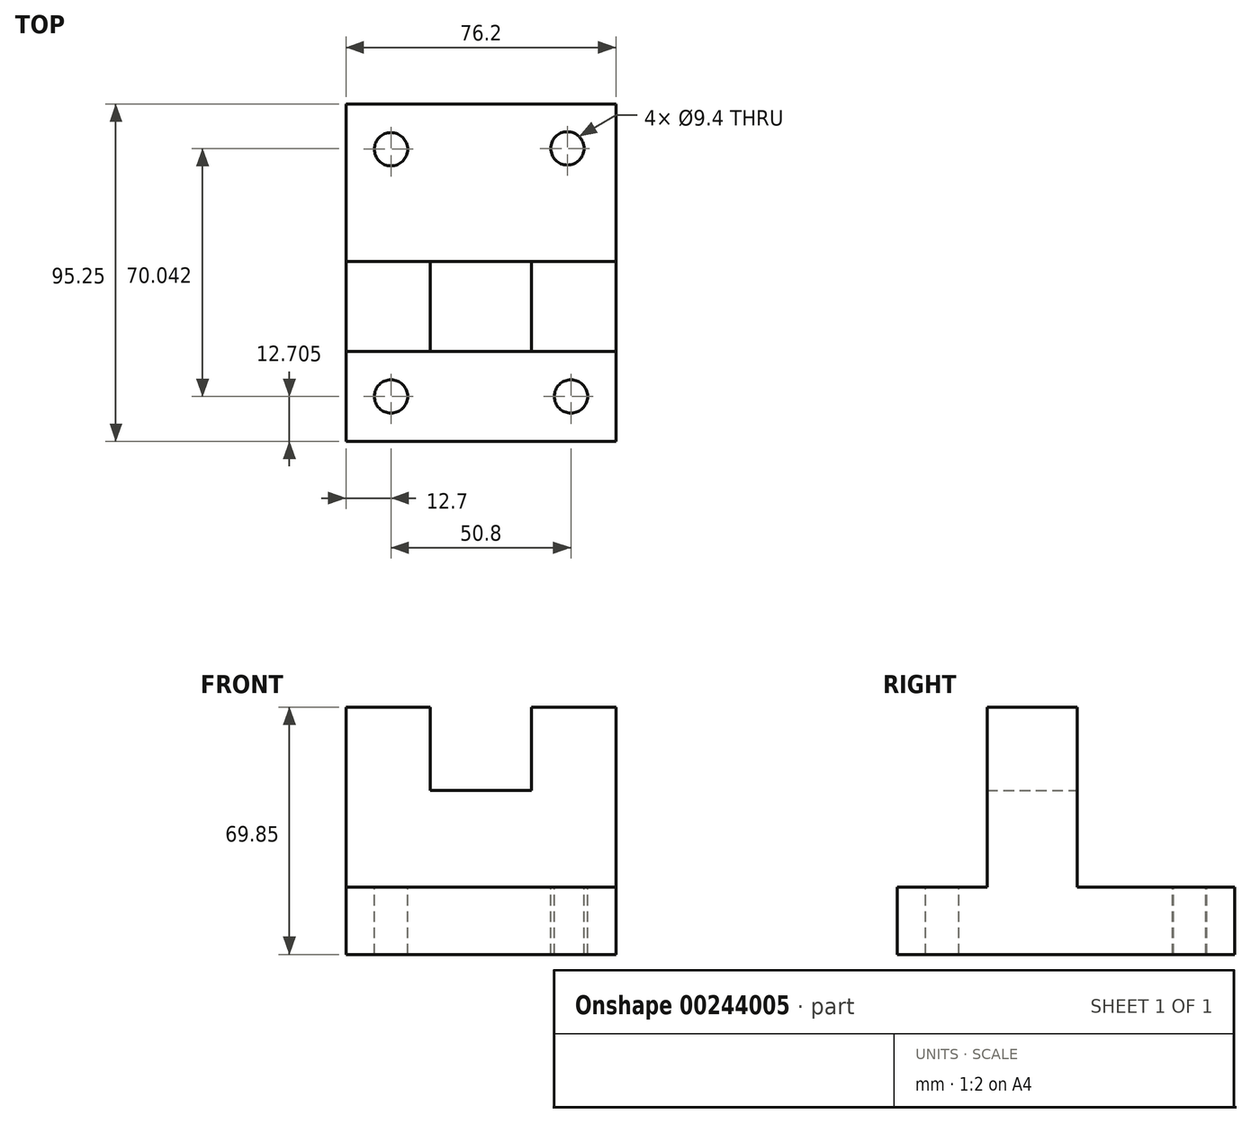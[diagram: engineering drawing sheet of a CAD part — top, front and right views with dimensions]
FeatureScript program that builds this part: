
annotation { "Feature Type Name" : "Feature", "Feature Type Description" : "" }
export const myFeature = defineFeature(function(context is Context, id is Id, definition is map)
    precondition{}
    {
        {
            var Q0;
            Q0=qCreatedBy(makeId("Right.planeOp"),FACE);
            var sketch = newSketch(context, id + "F0", { "sketchPlane" : qUnion([Q0])});
            skLineSegment(sketch, "E0", {"start": v(50.7, -32.28) * mm, "end": v(-44.55, -32.28) * mm});
            skLineSegment(sketch, "E1", {"start": v(-44.55, -32.28) * mm, "end": v(-44.55, -13.23) * mm});
            skLineSegment(sketch, "E2", {"start": v(50.7, -32.28) * mm, "end": v(50.7, -13.23) * mm});
            skLineSegment(sketch, "E3", {"start": v(50.7, -13.23) * mm, "end": v(6.25, -13.23) * mm});
            skLineSegment(sketch, "E4", {"start": v(6.25, -13.23) * mm, "end": v(6.25, 37.57) * mm});
            skLineSegment(sketch, "E5", {"start": v(6.25, 37.57) * mm, "end": v(-19.15, 37.57) * mm});
            skLineSegment(sketch, "E6", {"start": v(-19.15, 37.57) * mm, "end": v(-19.15, -13.23) * mm});
            skLineSegment(sketch, "E7", {"start": v(-19.15, -13.23) * mm, "end": v(-44.55, -13.23) * mm});
            skSolve(sketch);
        }
        {
            var Q0;
            Q0=makeQuery(id+"F0.imprint","IMPRINT",FACE,{"disambiguationData":[TD([[makeQuery(id+"F0.imprint","IMPRINT",EDGE,{"derivedFrom":sQuery(id+"F0.wireOp",EDGE,"E0")}),-1.0]])]});
            extrude(context, id + "F1", {"entities" : qUnion([Q0]), "depth" : 76.2 * mm});
        }
        {
            var Q0;
            Q0=makeQuery(id+"F1.opExtrude","SWEPT_FACE",FACE,{"disambiguationData":[OSD([sQuery(id+"F0.wireOp",EDGE,"E4")])]});
            var sketch = newSketch(context, id + "F2", { "sketchPlane" : qUnion([Q0])});
            skLineSegment(sketch, "E8.bottom", {"start": v(-23.81, 13.99) * mm, "end": v(-52.39, 13.99) * mm});
            skLineSegment(sketch, "E8.left", {"start": v(-23.81, 13.99) * mm, "end": v(-23.81, 37.57) * mm});
            skLineSegment(sketch, "E8.right", {"start": v(-52.39, 13.99) * mm, "end": v(-52.39, 37.57) * mm});
            skPoint(sketch, "E8.middle", {"position": v(-38.1, 37.57) * mm});
            skLineSegment(sketch, "E9", {"start": v(-52.39, 37.57) * mm, "end": v(-23.81, 37.57) * mm});
            skPoint(sketch, "E10.orphan", {"position": v(-52.39, 61.14) * mm});
            skPoint(sketch, "E11.orphan", {"position": v(-23.81, 61.14) * mm});
            skSolve(sketch);
        }
        {
            var Q0;
            Q0=makeQuery(id+"F2.imprint","IMPRINT",FACE,{"disambiguationData":[TD([[makeQuery(id+"F2.imprint","IMPRINT",EDGE,{"derivedFrom":sQuery(id+"F2.wireOp",EDGE,"E8.bottom")}),-1.0]])]});
            extrude(context, id + "F3", {"entities" : qUnion([Q0]), "operationType" : NewBodyOperationType.REMOVE, "endBound" : BoundingType.THROUGH_ALL, "oppositeDirection" : true, "depth" : 25.4 * mm});
        }
        {
            var Q0;
            Q0=makeQuery(id+"F1.opExtrude","SWEPT_FACE",FACE,{"disambiguationData":[OSD([sQuery(id+"F0.wireOp",EDGE,"E3")])]});
            var sketch = newSketch(context, id + "F4", { "sketchPlane" : qUnion([Q0])});
            skSolve(sketch);
        }
        {
            var Q0;
            {var subQ0=sQuery(id+"F0.wireOp",EDGE,"E3");Q0=makeQuery(id+"F4.imprint","IMPRINT",FACE,{"disambiguationData":[TD([[makeQuery(id+"F4.imprint","IMPRINT",EDGE,{"derivedFrom":makeQuery(id+"F1.opExtrude","CAP_EDGE",EDGE,{"disambiguationData":[OSD([subQ0])],"isStart":true})}),1.0]])]});}
            var sketch = newSketch(context, id + "F5", { "sketchPlane" : qUnion([Q0])});
            skLineSegment(sketch, "E12", {"start": v(0, 50.65) * mm, "end": v(12.7, 50.65) * mm});
            skLineSegment(sketch, "E13", {"start": v(12.7, 50.65) * mm, "end": v(12.7, 37.95) * mm});
            skSolve(sketch);
        }
        {
            var Q0;
            Q0=sQuery(id+"F5.wireOp",VERTEX,"E13.end");
            var Q1;
            Q1=makeQuery(id+"F1.opExtrude","SWEPT_BODY",BODY,{"disambiguationData":[OSD([sQuery(id+"F0.wireOp",EDGE,"E0"),sQuery(id+"F0.wireOp",EDGE,"E1"),sQuery(id+"F0.wireOp",EDGE,"E2"),sQuery(id+"F0.wireOp",EDGE,"E3"),sQuery(id+"F0.wireOp",EDGE,"E4"),sQuery(id+"F0.wireOp",EDGE,"E5"),sQuery(id+"F0.wireOp",EDGE,"E6"),sQuery(id+"F0.wireOp",EDGE,"E7")])]});
            hole(context, id + "F6", {"style" : HoleStyle.SIMPLE, "endStyle" : HoleEndStyle.THROUGH, "holeDiameter" : 9.4 * mm, "locations" : qUnion([Q0]), "scope" : qUnion([Q1]), "isTappedThrough" : true});
        }
        {
            var Q0;
            {var subQ0=sQuery(id+"F0.wireOp",EDGE,"E3");Q0=makeQuery(id+"F4.imprint","IMPRINT",FACE,{"disambiguationData":[TD([[makeQuery(id+"F4.imprint","IMPRINT",EDGE,{"derivedFrom":makeQuery(id+"F1.opExtrude","CAP_EDGE",EDGE,{"disambiguationData":[OSD([subQ0])],"isStart":true})}),1.0]])]});}
            var sketch = newSketch(context, id + "F7", { "sketchPlane" : qUnion([Q0])});
            skLineSegment(sketch, "E14", {"start": v(75.2, 50.9) * mm, "end": v(62.5, 50.9) * mm});
            skLineSegment(sketch, "E15", {"start": v(62.5, 50.9) * mm, "end": v(62.5, 38.2) * mm});
            skSolve(sketch);
        }
        {
            var Q0;
            Q0=sQuery(id+"F7.wireOp",VERTEX,"E15.end");
            var Q1;
            Q1=makeQuery(id+"F1.opExtrude","SWEPT_BODY",BODY,{"disambiguationData":[OSD([sQuery(id+"F0.wireOp",EDGE,"E0"),sQuery(id+"F0.wireOp",EDGE,"E1"),sQuery(id+"F0.wireOp",EDGE,"E2"),sQuery(id+"F0.wireOp",EDGE,"E3"),sQuery(id+"F0.wireOp",EDGE,"E4"),sQuery(id+"F0.wireOp",EDGE,"E5"),sQuery(id+"F0.wireOp",EDGE,"E6"),sQuery(id+"F0.wireOp",EDGE,"E7")])]});
            hole(context, id + "F8", {"style" : HoleStyle.SIMPLE, "endStyle" : HoleEndStyle.THROUGH, "holeDiameter" : 9.4 * mm, "locations" : qUnion([Q0]), "scope" : qUnion([Q1]), "isTappedThrough" : true});
        }
        {
            var Q0;
            Q0=makeQuery(id+"F1.opExtrude","SWEPT_FACE",FACE,{"disambiguationData":[OSD([sQuery(id+"F0.wireOp",EDGE,"E7")])]});
            var sketch = newSketch(context, id + "F9", { "sketchPlane" : qUnion([Q0])});
            skLineSegment(sketch, "E16", {"start": v(0, -44.55) * mm, "end": v(12.7, -44.55) * mm});
            skLineSegment(sketch, "E17", {"start": v(76.2, -44.55) * mm, "end": v(63.5, -44.55) * mm});
            skLineSegment(sketch, "E18", {"start": v(12.7, -44.55) * mm, "end": v(12.7, -31.85) * mm});
            skLineSegment(sketch, "E19", {"start": v(63.5, -44.55) * mm, "end": v(63.5, -31.85) * mm});
            skSolve(sketch);
        }
        {
            var Q0;
            Q0=sQuery(id+"F9.wireOp",VERTEX,"E18.end");
            var Q1;
            Q1=sQuery(id+"F9.wireOp",VERTEX,"E19.end");
            var Q2;
            Q2=makeQuery(id+"F1.opExtrude","SWEPT_BODY",BODY,{"disambiguationData":[OSD([sQuery(id+"F0.wireOp",EDGE,"E0"),sQuery(id+"F0.wireOp",EDGE,"E1"),sQuery(id+"F0.wireOp",EDGE,"E2"),sQuery(id+"F0.wireOp",EDGE,"E3"),sQuery(id+"F0.wireOp",EDGE,"E4"),sQuery(id+"F0.wireOp",EDGE,"E5"),sQuery(id+"F0.wireOp",EDGE,"E6"),sQuery(id+"F0.wireOp",EDGE,"E7")])]});
            hole(context, id + "F10", {"style" : HoleStyle.SIMPLE, "endStyle" : HoleEndStyle.THROUGH, "holeDiameter" : 9.4 * mm, "locations" : qUnion([Q0, Q1]), "scope" : qUnion([Q2]), "isTappedThrough" : true});
        }
    });
